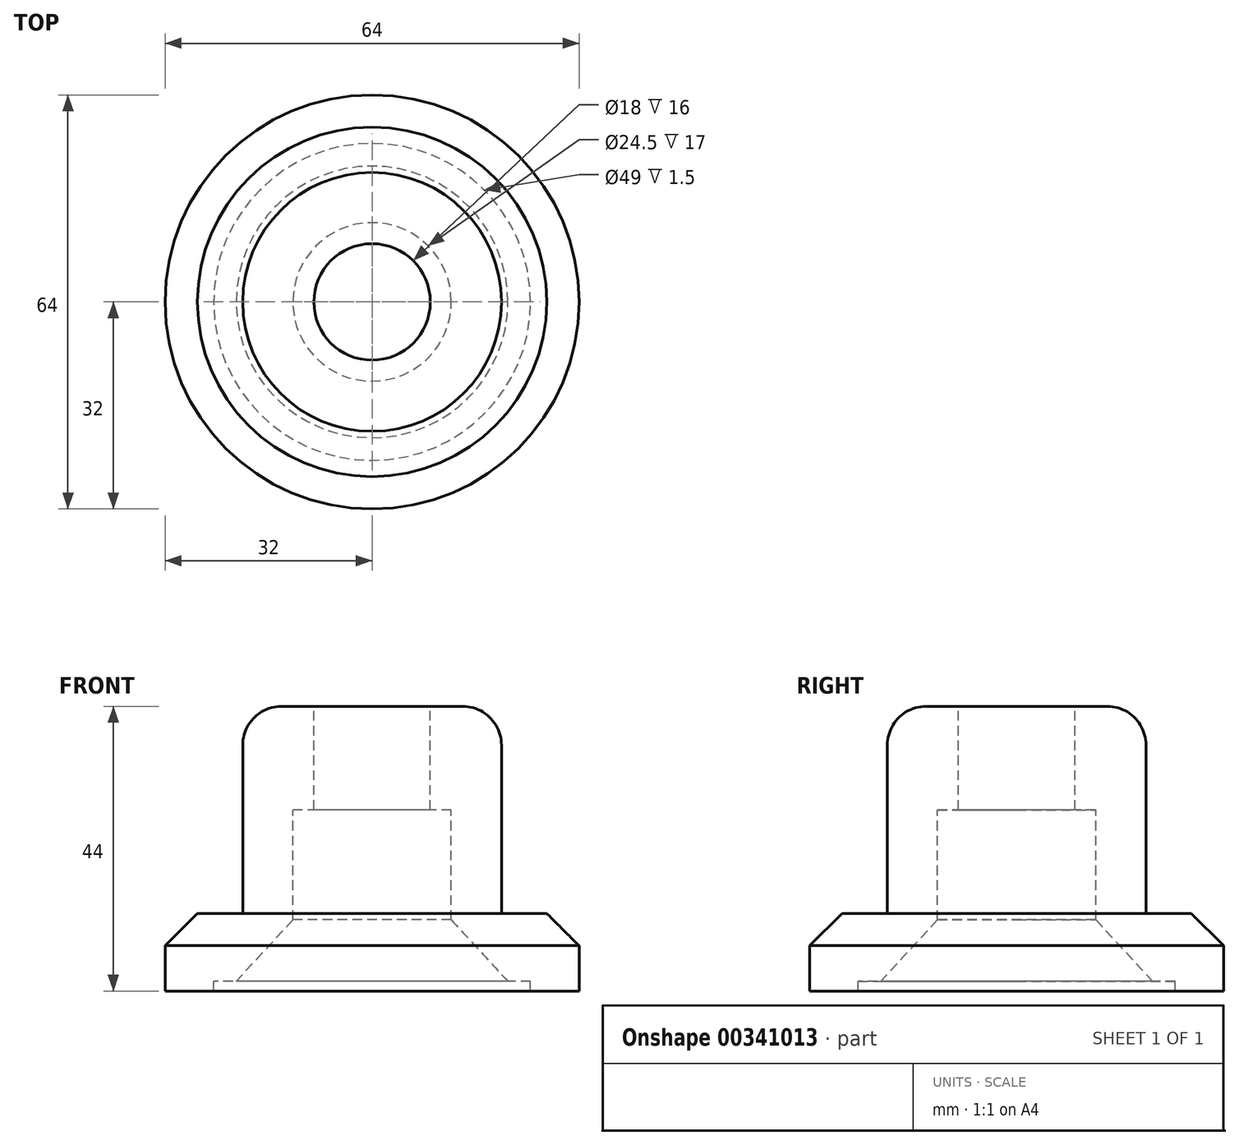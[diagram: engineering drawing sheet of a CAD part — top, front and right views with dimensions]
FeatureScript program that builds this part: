
annotation { "Feature Type Name" : "Feature", "Feature Type Description" : "" }
export const myFeature = defineFeature(function(context is Context, id is Id, definition is map)
    precondition{}
    {
        {
            var Q0;
            Q0=qCreatedBy(makeId("Front.planeOp"),FACE);
            var sketch = newSketch(context, id + "F0", { "sketchPlane" : qUnion([Q0])});
            skLineSegment(sketch, "E0", {"start": v(9, 22) * mm, "end": v(14, 22) * mm});
            skLineSegment(sketch, "E1", {"start": v(20, 16) * mm, "end": v(20, -10) * mm});
            skArc(sketch, "E2.filletArc", {"start": v(20, 16) * mm, "mid": v(18.24, 20.24) * mm, "end": v(14, 22) * mm});
            skLineSegment(sketch, "E3", {"start": v(20, -10) * mm, "end": v(27, -10) * mm});
            skLineSegment(sketch, "E4", {"start": v(24.5, -22) * mm, "end": v(32, -22) * mm});
            skLineSegment(sketch, "E5", {"start": v(32, -22) * mm, "end": v(32, -15) * mm});
            skLineSegment(sketch, "E6", {"start": v(32, -15) * mm, "end": v(27, -10) * mm});
            skLineSegment(sketch, "E7.trimOffspring", {"start": v(32, -10) * mm, "end": v(50, -10) * mm, "construction": true});
            skLineSegment(sketch, "E8", {"start": v(9, 22) * mm, "end": v(9, 6) * mm});
            skLineSegment(sketch, "E9", {"start": v(9, 6) * mm, "end": v(12.25, 6) * mm});
            skLineSegment(sketch, "E10", {"start": v(12.25, 6) * mm, "end": v(12.25, -11) * mm});
            skLineSegment(sketch, "E11", {"start": v(24.5, -22) * mm, "end": v(24.5, -20.5) * mm});
            skLineSegment(sketch, "E12", {"start": v(24.5, -20.5) * mm, "end": v(21, -20.5) * mm});
            skLineSegment(sketch, "E13", {"start": v(21, -20.5) * mm, "end": v(12.25, -11) * mm});
            skLineSegment(sketch, "E14", {"start": v(0, 31.24) * mm, "end": v(0, -32.53) * mm, "construction": true});
            skSolve(sketch);
        }
        {
            var Q0;
            Q0=makeQuery(id+"F0.imprint","IMPRINT",FACE,{"disambiguationData":[TD([[makeQuery(id+"F0.imprint","IMPRINT",EDGE,{"derivedFrom":sQuery(id+"F0.wireOp",EDGE,"E0")}),-1.0]])]});
            var Q1;
            Q1=sQuery(id+"F0.wireOp",EDGE,"E14");
            revolve(context, id + "F1", {"entities" : qUnion([Q0]), "axis" : qUnion([Q1]), "revolveType" : RevolveType.FULL});
        }
    });
